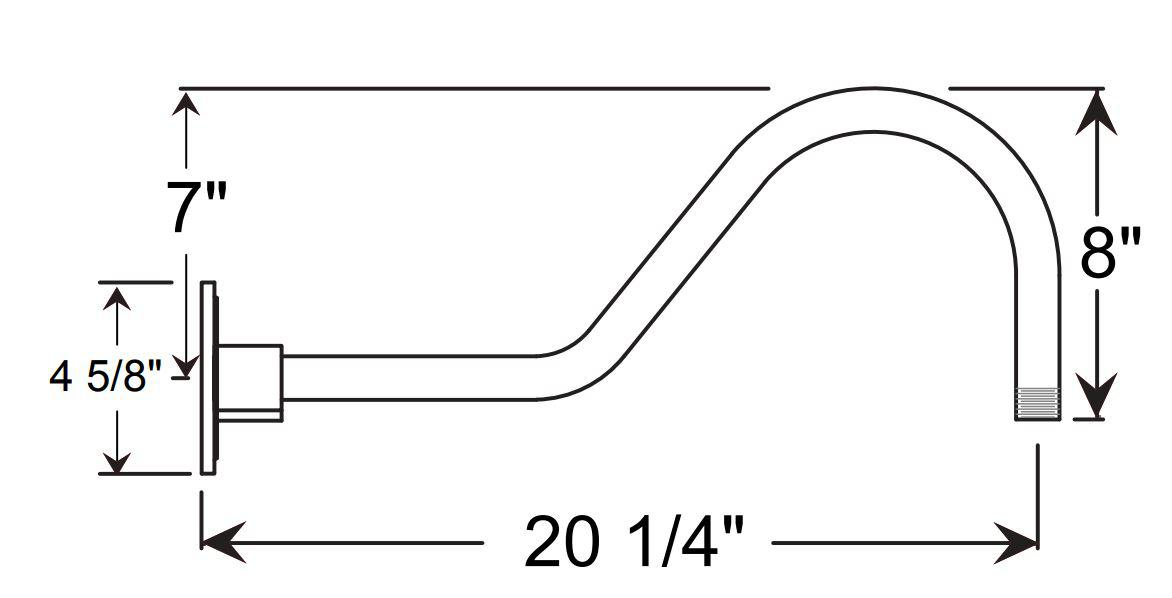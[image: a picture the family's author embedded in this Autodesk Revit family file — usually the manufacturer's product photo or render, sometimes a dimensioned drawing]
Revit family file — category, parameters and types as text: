
# Revit family: Warehouse DeepLED 20,24,27,30,36,42
name_source: partatom
category: Lighting Fixtures
units: mm (PartAtom-declared; Revit-internal decimal feet)

## family parameters
Always vertical = Yes
Cut with Voids When Loaded = No
Light Source = Yes
OmniClass Number = 23.80.70.00
OmniClass Title = Lighting
Part Type = Normal
Room Calculation Point = No
Round Connector Dimension = Use Diameter
Shared = No
Work Plane-Based = No

## types (6) — shared parameters
Body Colour = Spun aluminium
Body Material = body
CRI = >90
Color Filter = 16777215
Construction Material = Heavy Duty spun aluminum.
Default Elevation = 0' - 0"
Description = 120-277 Voltage
Dimming = 1%
Dimming Lamp Color Temperature Shift = <None>
Efficiency = 65-125 lumens per watt
Lamp = LED
Life = L70 50,000 hours
Load Classification = Lighting
Manufacturer = ANP Lighting
Photometric Web File = generic
Power Factor = 1
Tilt Angle = 90.00°
URL = https://www.anplighting.com
Voltage = 277 V
Warranty = 5 year limited warranty

## per-type parameters (varying)
| type | Apparent Load | BULB | Bulb | Fixture Diameter | Fixture Height | OSWD524 | OSWD527 | OSWD530 | OSWD536 | OSWD542 | WD520 | Wattage Comments | Weight | a | b |
| OSWD524 | 24 VA | Yes | Bulb | 2' - 0" | 1' - 1" | Yes | No | No | No | No | No | 24W | 13.0 lbs | 1' - 1" | 0' - 1" |
| OSWD527 | 24 VA | Yes | Bulb | 2' - 3" | 1' - 3" | No | Yes | No | No | No | No | 24W | 15.0lbs | 1' - 3" | 0' - 2" |
| OSWD530 | 24 VA | Yes | Bulb | 2' - 6" | 1' - 3" | No | No | Yes | No | No | No | 24 W | 18.0 lbs | 1' - 3" | 0' - 2" |
| OSWD536 | 24 VA | Yes | Bulb | 3' - 0" | 1' - 6" | No | No | No | Yes | No | No | 24 W | 24.5lb | 1' - 6" | 0' - 4" |
| OSWD542 | 24 VA | Yes | Bulb | 3' - 6" | 1' - 9" | No | No | No | No | Yes | No | 24 W | 30.5 lbs | 1' - 9" | 0' - 6" |
| WD520 | 37 VA | No | <By Category> | 1' - 9" | 1' - 1 1/2" | No | No | No | No | No | Yes | 37 W | 3.0 lb | 1' - 1 1/2" | 0' - 2" |

note: column(s) folded — value = type name in every type: Model

## geometry (parser evidence)
native form markers: Sweep x51
no freeform markers — native parametric forms only
